AUTODESK INVENTOR PART (.ipt)
format: ipt  version: 2017 (Build 210142000, 142)  size: 126,464 bytes
history: native  units: mm
features: other x3, plane x2, sketch x2, sweep x1, reference x1
ambient origin geometry x8: Origin, YZ Plane, XZ Plane, XY Plane, X Axis, Y Axis, Z Axis, Center Point
bodies: Solid1 (feature_tree)
feature tree (9):
  plane  "Work Plane2"
  sketch  "3D Sketch1"
  plane  "Work Plane3"
  sweep  "Sweep1"
  sketch  "Sketch2"  dims[d1=8.0mm d2=0.0mm d3=0.0mm]
  reference  "Reference2"
  other  "<userpath>\OneDrive\Inventor\VolledigGeassembleerdv001.iam"
  other  "VolledigGeassembleerdv001.iam"
  other  "winch:1"
